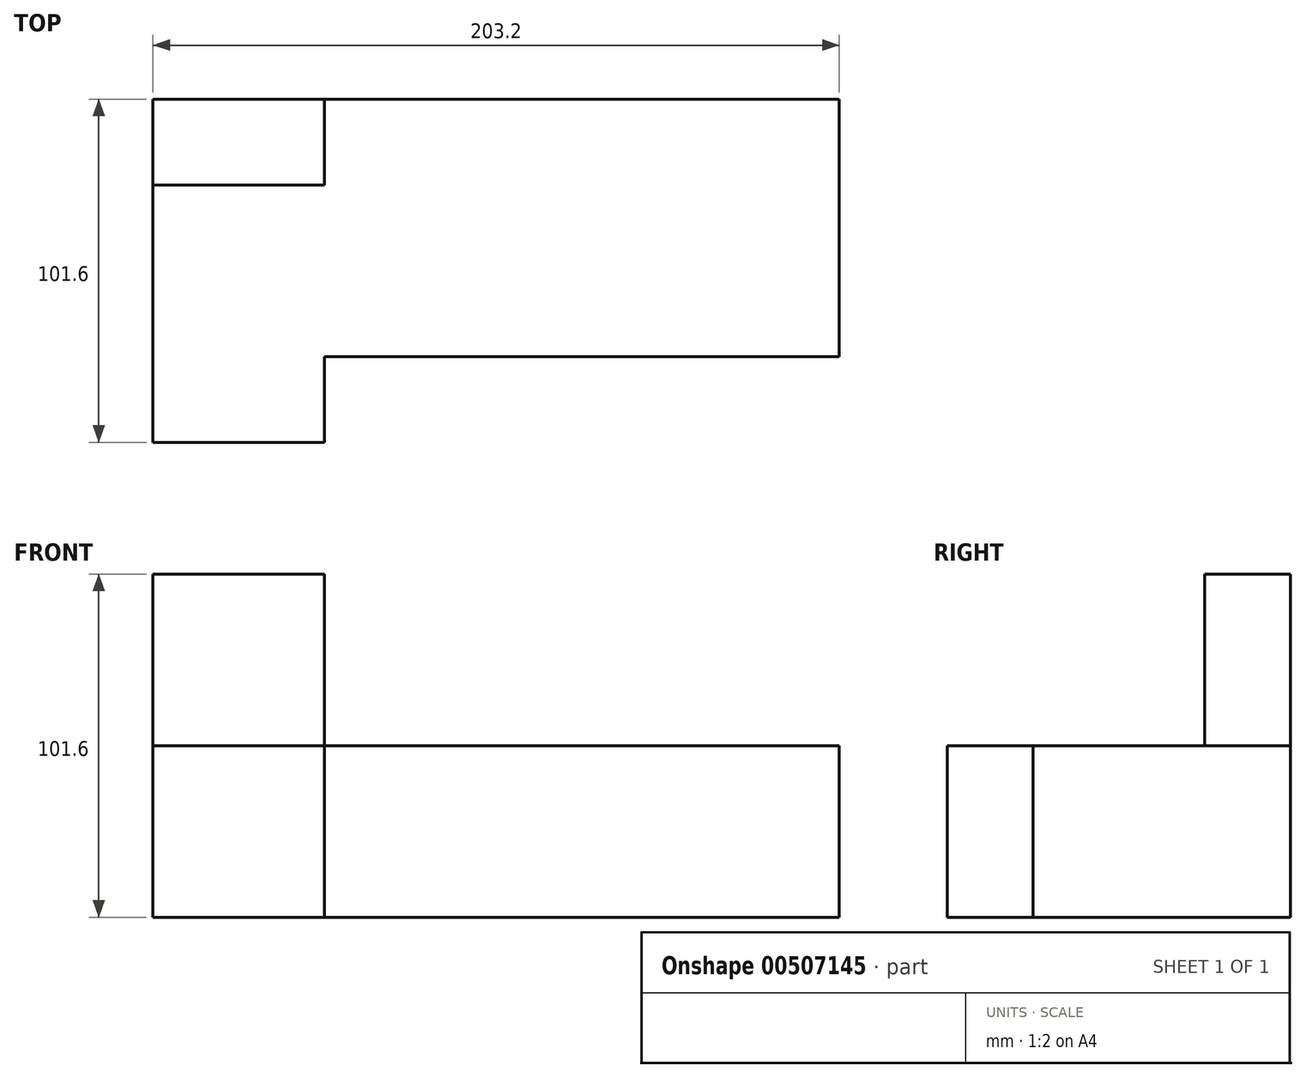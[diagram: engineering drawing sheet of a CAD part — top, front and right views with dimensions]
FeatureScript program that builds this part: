
annotation { "Feature Type Name" : "Feature", "Feature Type Description" : "" }
export const myFeature = defineFeature(function(context is Context, id is Id, definition is map)
    precondition{}
    {
        {
            var Q0;
            Q0=qCreatedBy(makeId("Front.planeOp"),FACE);
            var sketch = newSketch(context, id + "F0", { "sketchPlane" : qUnion([Q0])});
            skLineSegment(sketch, "E0.bottom", {"start": v(0, 0) * mm, "end": v(-203.2, 0) * mm});
            skLineSegment(sketch, "E0.top", {"start": v(0, 50.8) * mm, "end": v(-203.2, 50.8) * mm});
            skLineSegment(sketch, "E0.left", {"start": v(0, 0) * mm, "end": v(0, 50.8) * mm});
            skLineSegment(sketch, "E0.right", {"start": v(-203.2, 0) * mm, "end": v(-203.2, 50.8) * mm});
            skSolve(sketch);
        }
        {
            var Q0;
            Q0 = qSketchRegion(id + "F0", true);
            var Q1;
            Q1=makeQuery(id+"F0.imprint","IMPRINT",FACE,{"disambiguationData":[TD([[makeQuery(id+"F0.imprint","IMPRINT",EDGE,{"derivedFrom":sQuery(id+"F0.wireOp",EDGE,"E0.bottom")}),-1.0]])]});
            extrude(context, id + "F1", {"entities" : qUnion([Q0, Q1]), "depth" : 101.6 * mm});
        }
        {
            var Q0;
            Q0=makeQuery(id+"F1.opExtrude","CAP_FACE",FACE,{"disambiguationData":[OSD([sQuery(id+"F0.wireOp",EDGE,"E0.bottom"),sQuery(id+"F0.wireOp",EDGE,"E0.top"),sQuery(id+"F0.wireOp",EDGE,"E0.left"),sQuery(id+"F0.wireOp",EDGE,"E0.right")])],"isStart":false});
            var sketch = newSketch(context, id + "F2", { "sketchPlane" : qUnion([Q0])});
            skLineSegment(sketch, "E1.bottom", {"start": v(0, 0) * mm, "end": v(-152.4, 0) * mm});
            skLineSegment(sketch, "E1.top", {"start": v(0, 50.8) * mm, "end": v(-152.4, 50.8) * mm});
            skLineSegment(sketch, "E1.left", {"start": v(0, 0) * mm, "end": v(0, 50.8) * mm});
            skLineSegment(sketch, "E1.right", {"start": v(-152.4, 0) * mm, "end": v(-152.4, 50.8) * mm});
            skSolve(sketch);
        }
        {
            var Q0;
            Q0 = qSketchRegion(id + "F2", true);
            extrude(context, id + "F3", {"entities" : qUnion([Q0]), "operationType" : NewBodyOperationType.REMOVE, "oppositeDirection" : true, "depth" : 25.4 * mm});
        }
        {
            var Q0;
            Q0=makeQuery(id+"F1.opExtrude","SWEPT_FACE",FACE,{"disambiguationData":[OSD([sQuery(id+"F0.wireOp",EDGE,"E0.top")])]});
            var sketch = newSketch(context, id + "F4", { "sketchPlane" : qUnion([Q0])});
            skLineSegment(sketch, "E2.bottom", {"start": v(-203.2, 0) * mm, "end": v(-152.4, 0) * mm});
            skLineSegment(sketch, "E2.top", {"start": v(-203.2, -25.4) * mm, "end": v(-152.4, -25.4) * mm});
            skLineSegment(sketch, "E2.left", {"start": v(-203.2, 0) * mm, "end": v(-203.2, -25.4) * mm});
            skLineSegment(sketch, "E2.right", {"start": v(-152.4, 0) * mm, "end": v(-152.4, -25.4) * mm});
            skSolve(sketch);
        }
        {
            var Q0;
            Q0 = qSketchRegion(id + "F4", true);
            var Q1;
            Q1=makeQuery(id+"F4.imprint","IMPRINT",FACE,{"disambiguationData":[TD([[makeQuery(id+"F4.imprint","IMPRINT",EDGE,{"derivedFrom":sQuery(id+"F4.wireOp",EDGE,"E2.bottom")}),1.0]])]});
            extrude(context, id + "F5", {"entities" : qUnion([Q0, Q1]), "operationType" : NewBodyOperationType.ADD, "depth" : 50.8 * mm});
        }
    });
